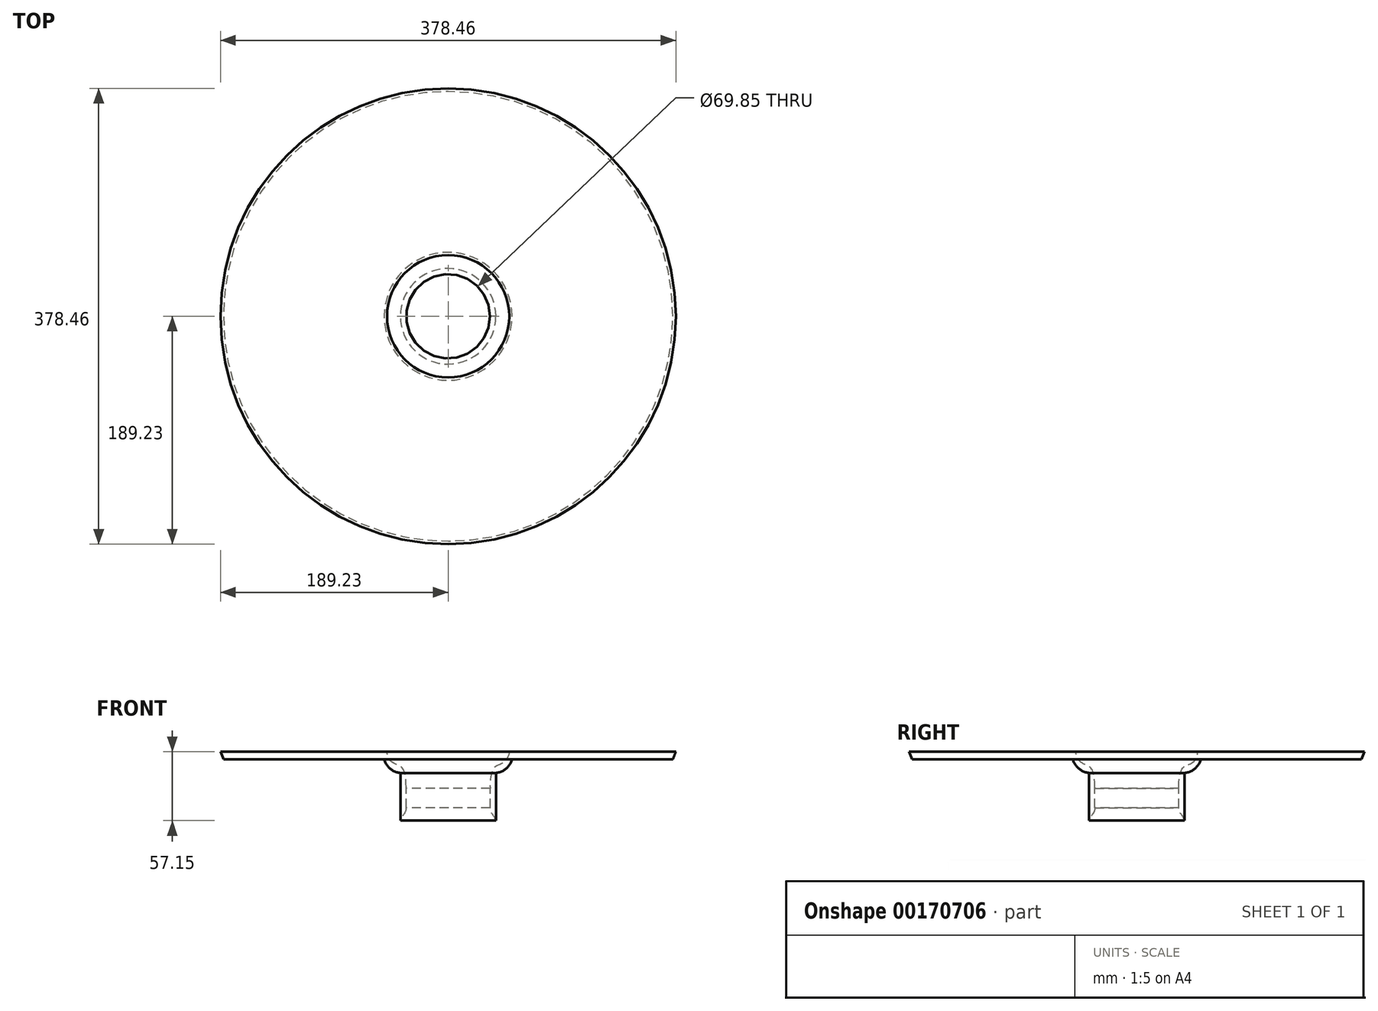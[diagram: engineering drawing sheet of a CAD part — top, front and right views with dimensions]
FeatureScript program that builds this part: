
annotation { "Feature Type Name" : "Feature", "Feature Type Description" : "" }
export const myFeature = defineFeature(function(context is Context, id is Id, definition is map)
    precondition{}
    {
        {
            var Q0;
            Q0=qCreatedBy(makeId("Front.planeOp"),FACE);
            var sketch = newSketch(context, id + "F0", { "sketchPlane" : qUnion([Q0])});
            skLineSegment(sketch, "E0", {"start": v(53.14, 0) * mm, "end": v(186.7, 0) * mm});
            skLineSegment(sketch, "E1", {"start": v(186.7, 0) * mm, "end": v(189.23, 6.35) * mm});
            skLineSegment(sketch, "E2", {"start": v(189.23, 6.35) * mm, "end": v(50.8, 6.35) * mm});
            skLineSegment(sketch, "E3", {"start": v(39.69, -11.25) * mm, "end": v(39.69, -50.8) * mm});
            skLineSegment(sketch, "E4", {"start": v(34.93, -40.06) * mm, "end": v(34.93, -23.9) * mm});
            skPoint(sketch, "E5.visualSharp", {"position": v(34.93, -23.9) * mm});
            skArc(sketch, "E6", {"start": v(39.69, -11.25) * mm, "mid": v(48.15, -7.7) * mm, "end": v(53.14, 0) * mm});
            skLineSegment(sketch, "E7", {"start": v(0, 59.49) * mm, "end": v(0, -54.68) * mm, "construction": true});
            skFitSpline(sketch, "E8", {"points": [v(50.8, 6.35) * mm, v(39.3, -5.95) * mm, v(34.93, -23.9) * mm], "startDerivative": vector(-10, -66.16) * mm, "endDerivative": vector(0.6, -46.18) * mm});
            skFitSpline(sketch, "E9", {"points": [v(39.69, -50.8) * mm, v(34.93, -40.06) * mm], "startDerivative": vector(-4.22, 14.92) * mm, "endDerivative": vector(0.17, 14.68) * mm});
            skSolve(sketch);
        }
        {
            var Q0;
            Q0=makeQuery(id+"F0.imprint","IMPRINT",FACE,{"disambiguationData":[TD([[makeQuery(id+"F0.imprint","IMPRINT",EDGE,{"derivedFrom":sQuery(id+"F0.wireOp",EDGE,"E0")}),1.0]])]});
            var Q1;
            Q1=sQuery(id+"F0.wireOp",EDGE,"E7");
            revolve(context, id + "F1", {"entities" : qUnion([Q0]), "axis" : qUnion([Q1]), "revolveType" : RevolveType.FULL});
        }
    });
